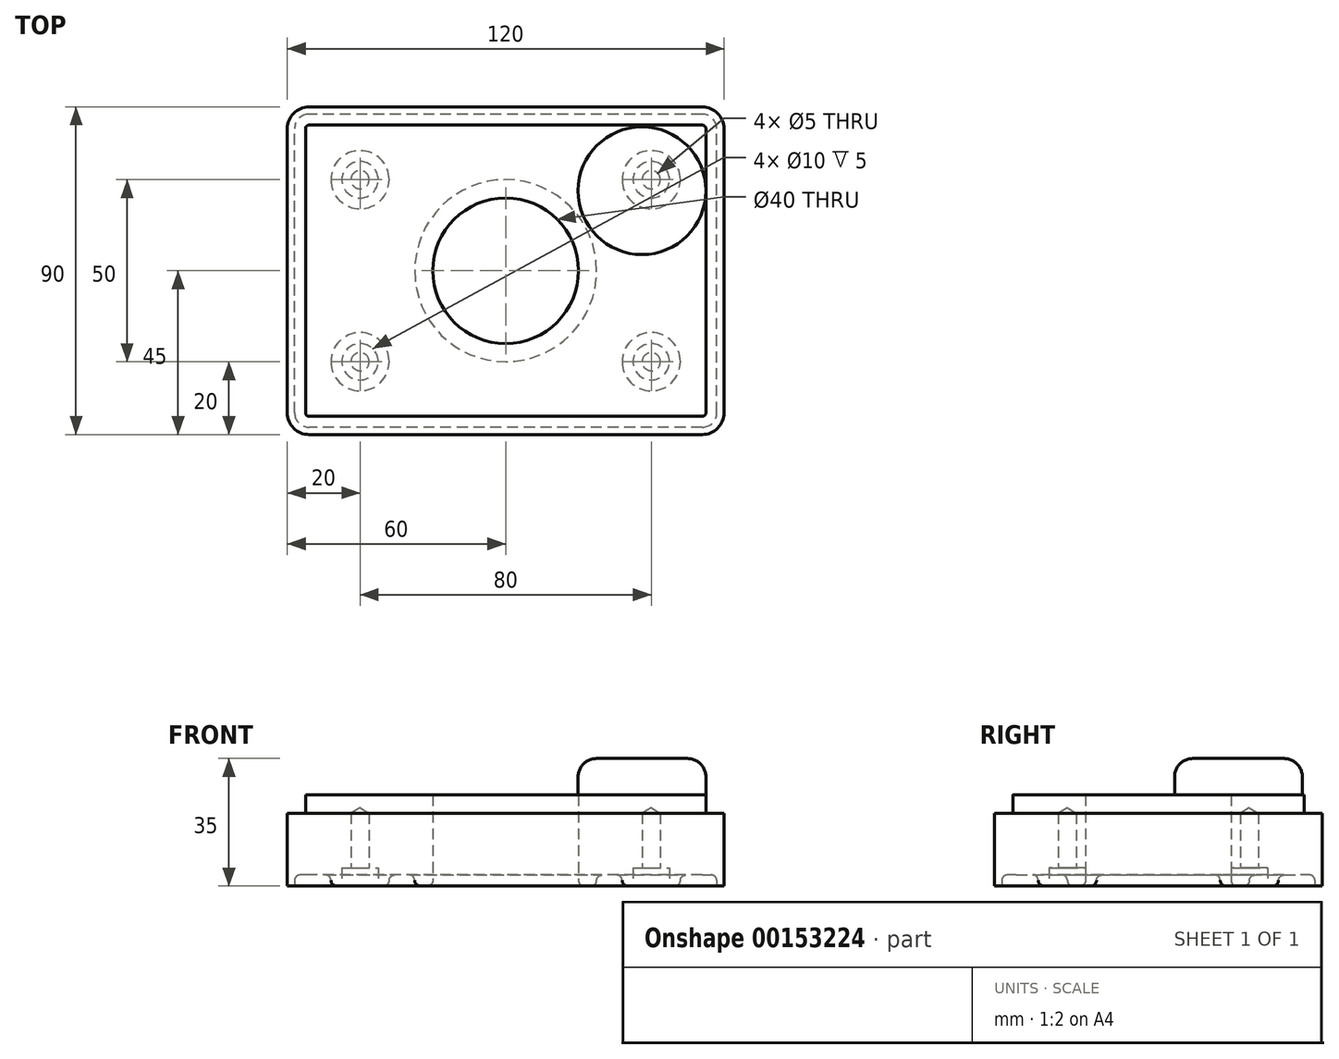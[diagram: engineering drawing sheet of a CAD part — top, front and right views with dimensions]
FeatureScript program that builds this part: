
annotation { "Feature Type Name" : "Feature", "Feature Type Description" : "" }
export const myFeature = defineFeature(function(context is Context, id is Id, definition is map)
    precondition{}
    {
        {
            var Q0;
            Q0=qCreatedBy(makeId("Top.planeOp"),FACE);
            var sketch = newSketch(context, id + "F11", { "sketchPlane" : qUnion([Q0])});
            skLineSegment(sketch, "E0.bottom", {"start": v(54, -45) * mm, "end": v(-54, -45) * mm});
            skLineSegment(sketch, "E0.top", {"start": v(54, 45) * mm, "end": v(-54, 45) * mm});
            skLineSegment(sketch, "E0.left", {"start": v(60, -39) * mm, "end": v(60, 39) * mm});
            skLineSegment(sketch, "E0.right", {"start": v(-60, -39) * mm, "end": v(-60, 39) * mm});
            skPoint(sketch, "E0.middle", {"position": v(0, 0) * mm});
            skCircle(sketch, "E1", {"center": v(0, 0) * mm, "radius": 20 * mm});
            skPoint(sketch, "E2.visualSharp", {"position": v(-60, -45) * mm});
            skArc(sketch, "E2.filletArc", {"start": v(-60, -39) * mm, "mid": v(-58.24, -43.24) * mm, "end": v(-54, -45) * mm});
            skPoint(sketch, "E3.visualSharp", {"position": v(60, -45) * mm});
            skArc(sketch, "E3.filletArc", {"start": v(54, -45) * mm, "mid": v(58.24, -43.24) * mm, "end": v(60, -39) * mm});
            skPoint(sketch, "E4.visualSharp", {"position": v(60, 45) * mm});
            skArc(sketch, "E4.filletArc", {"start": v(60, 39) * mm, "mid": v(58.24, 43.24) * mm, "end": v(54, 45) * mm});
            skPoint(sketch, "E5.visualSharp", {"position": v(-60, 45) * mm});
            skArc(sketch, "E5.filletArc", {"start": v(-54, 45) * mm, "mid": v(-58.24, 43.24) * mm, "end": v(-60, 39) * mm});
            skSolve(sketch);
        }
        {
            var Q0;
            Q0=makeQuery(id+"F11.imprint","IMPRINT",FACE,{"disambiguationData":[TD([[makeQuery(id+"F11.imprint","IMPRINT",EDGE,{"derivedFrom":sQuery(id+"F11.wireOp",EDGE,"E0.bottom")}),-1.0]])]});
            extrude(context, id + "F0", {"entities" : qUnion([Q0]), "depth" : 25 * mm});
        }
        {
            var Q0;
            Q0=makeQuery(id+"F0.opExtrude","CAP_FACE",FACE,{"disambiguationData":[OSD([sQuery(id+"F11.wireOp",EDGE,"E0.bottom"),sQuery(id+"F11.wireOp",EDGE,"E0.top"),sQuery(id+"F11.wireOp",EDGE,"E0.left"),sQuery(id+"F11.wireOp",EDGE,"E0.right"),sQuery(id+"F11.wireOp",EDGE,"E1"),sQuery(id+"F11.wireOp",EDGE,"E2.filletArc"),sQuery(id+"F11.wireOp",EDGE,"E3.filletArc"),sQuery(id+"F11.wireOp",EDGE,"E4.filletArc"),sQuery(id+"F11.wireOp",EDGE,"E5.filletArc")])],"isStart":false});
            var sketch = newSketch(context, id + "F1", { "sketchPlane" : qUnion([Q0])});
            skArc(sketch, "E6.0", {"start": v(54, -40) * mm, "mid": v(54.7, -39.7) * mm, "end": v(55, -39) * mm});
            skLineSegment(sketch, "E6.1", {"start": v(55, -39) * mm, "end": v(55, 39) * mm});
            skLineSegment(sketch, "E6.2", {"start": v(54, -40) * mm, "end": v(-54, -40) * mm});
            skArc(sketch, "E6.3", {"start": v(55, 39) * mm, "mid": v(54.7, 39.7) * mm, "end": v(54, 40) * mm});
            skArc(sketch, "E6.4", {"start": v(-55, -39) * mm, "mid": v(-54.7, -39.7) * mm, "end": v(-54, -40) * mm});
            skLineSegment(sketch, "E6.5", {"start": v(-55, -39) * mm, "end": v(-55, 39) * mm});
            skArc(sketch, "E6.6", {"start": v(-54, 40) * mm, "mid": v(-54.7, 39.7) * mm, "end": v(-55, 39) * mm});
            skLineSegment(sketch, "E6.7", {"start": v(54, 40) * mm, "end": v(-54, 40) * mm});
            skSolve(sketch);
        }
        {
            var Q0;
            Q0=makeQuery(id+"F1.imprint","IMPRINT",FACE,{"disambiguationData":[TD([[makeQuery(id+"F1.imprint","IMPRINT",EDGE,{"derivedFrom":sQuery(id+"F1.wireOp",EDGE,"E6.0")}),-1.0]])]});
            extrude(context, id + "F2", {"entities" : qUnion([Q0]), "operationType" : NewBodyOperationType.REMOVE, "oppositeDirection" : true, "depth" : 5 * mm});
        }
        {
            var Q0;
            Q0=makeQuery(id+"F0.opExtrude","CAP_FACE",FACE,{"disambiguationData":[OSD([sQuery(id+"F11.wireOp",EDGE,"E0.bottom"),sQuery(id+"F11.wireOp",EDGE,"E0.top"),sQuery(id+"F11.wireOp",EDGE,"E0.left"),sQuery(id+"F11.wireOp",EDGE,"E0.right"),sQuery(id+"F11.wireOp",EDGE,"E1"),sQuery(id+"F11.wireOp",EDGE,"E2.filletArc"),sQuery(id+"F11.wireOp",EDGE,"E3.filletArc"),sQuery(id+"F11.wireOp",EDGE,"E4.filletArc"),sQuery(id+"F11.wireOp",EDGE,"E5.filletArc")])],"isStart":true});
            var sketch = newSketch(context, id + "F3", { "sketchPlane" : qUnion([Q0])});
            skPoint(sketch, "E7", {"position": v(40, -25) * mm});
            skPoint(sketch, "E8", {"position": v(-40, -25) * mm});
            skPoint(sketch, "E9", {"position": v(-40, 25) * mm});
            skPoint(sketch, "E10", {"position": v(40, 25) * mm});
            skLineSegment(sketch, "E11", {"start": v(40, -25) * mm, "end": v(40, 0) * mm, "construction": true});
            skLineSegment(sketch, "E12", {"start": v(40, 0) * mm, "end": v(40, 0) * mm});
            skLineSegment(sketch, "E13", {"start": v(40, 25) * mm, "end": v(40, 0) * mm, "construction": true});
            skLineSegment(sketch, "E14", {"start": v(40, 0) * mm, "end": v(0, 0) * mm, "construction": true});
            skLineSegment(sketch, "E15", {"start": v(40, -25) * mm, "end": v(-40, 25) * mm, "construction": true});
            skSolve(sketch);
        }
        {
            var Q0;
            Q0=sQuery(id+"F3.wireOp",VERTEX,"E7");
            var Q1;
            Q1=sQuery(id+"F3.wireOp",VERTEX,"E8");
            var Q2;
            Q2=sQuery(id+"F3.wireOp",VERTEX,"E9");
            var Q3;
            Q3=sQuery(id+"F3.wireOp",VERTEX,"E10");
            var Q4;
            Q4=makeQuery(id+"F0.opExtrude","SWEPT_BODY",BODY,{"disambiguationData":[OSD([sQuery(id+"F11.wireOp",EDGE,"E0.bottom"),sQuery(id+"F11.wireOp",EDGE,"E0.top"),sQuery(id+"F11.wireOp",EDGE,"E0.left"),sQuery(id+"F11.wireOp",EDGE,"E0.right"),sQuery(id+"F11.wireOp",EDGE,"E1"),sQuery(id+"F11.wireOp",EDGE,"E2.filletArc"),sQuery(id+"F11.wireOp",EDGE,"E3.filletArc"),sQuery(id+"F11.wireOp",EDGE,"E4.filletArc"),sQuery(id+"F11.wireOp",EDGE,"E5.filletArc")])]});
            hole(context, id + "F12", {"style" : HoleStyle.C_BORE, "endStyle" : HoleEndStyle.BLIND, "standardTappedOrClearance" : lookupTablePath({ "standard" : "ISO", "size" : "M5", "type" : "Tapped" }), "standardBlindInLast" : lookupTablePath({ "standard" : "ISO", "size" : "M5", "type" : "Tapped" }), "holeDiameter" : 5 * mm, "cBoreDiameter" : 10 * mm, "cBoreDepth" : 5 * mm, "holeDepth" : 20 * mm, "locations" : qUnion([Q0, Q1, Q2, Q3]), "scope" : qUnion([Q4])});
        }
        {
            var Q0;
            Q0=makeQuery(id+"F0.opExtrude","CAP_FACE",FACE,{"disambiguationData":[OSD([sQuery(id+"F11.wireOp",EDGE,"E0.bottom"),sQuery(id+"F11.wireOp",EDGE,"E0.top"),sQuery(id+"F11.wireOp",EDGE,"E0.left"),sQuery(id+"F11.wireOp",EDGE,"E0.right"),sQuery(id+"F11.wireOp",EDGE,"E1"),sQuery(id+"F11.wireOp",EDGE,"E2.filletArc"),sQuery(id+"F11.wireOp",EDGE,"E3.filletArc"),sQuery(id+"F11.wireOp",EDGE,"E4.filletArc"),sQuery(id+"F11.wireOp",EDGE,"E5.filletArc")])],"isStart":true});
            var sketch = newSketch(context, id + "F4", { "sketchPlane" : qUnion([Q0])});
            skCircle(sketch, "E16.0", {"center": v(0, 0) * mm, "radius": 25 * mm});
            skCircle(sketch, "E17.0", {"center": v(-40, 25) * mm, "radius": 8 * mm});
            skCircle(sketch, "E18.0", {"center": v(40, 25) * mm, "radius": 8 * mm});
            skCircle(sketch, "E19.0", {"center": v(40, -25) * mm, "radius": 8 * mm});
            skCircle(sketch, "E20.0", {"center": v(-40, -25) * mm, "radius": 8 * mm});
            skArc(sketch, "E21.0", {"start": v(54, 43) * mm, "mid": v(56.83, 41.83) * mm, "end": v(58, 39) * mm});
            skLineSegment(sketch, "E21.1", {"start": v(58, 39) * mm, "end": v(58, -39) * mm});
            skLineSegment(sketch, "E21.2", {"start": v(54, 43) * mm, "end": v(-54, 43) * mm});
            skArc(sketch, "E21.3", {"start": v(58, -39) * mm, "mid": v(56.83, -41.83) * mm, "end": v(54, -43) * mm});
            skArc(sketch, "E21.4", {"start": v(-58, 39) * mm, "mid": v(-56.83, 41.83) * mm, "end": v(-54, 43) * mm});
            skLineSegment(sketch, "E21.5", {"start": v(-58, 39) * mm, "end": v(-58, -39) * mm});
            skArc(sketch, "E21.6", {"start": v(-54, -43) * mm, "mid": v(-56.83, -41.83) * mm, "end": v(-58, -39) * mm});
            skLineSegment(sketch, "E21.7", {"start": v(54, -43) * mm, "end": v(-54, -43) * mm});
            skSolve(sketch);
        }
        {
            var Q0;
            Q0 = qSketchRegion(id + "F4", true);
            extrude(context, id + "F5", {"entities" : qUnion([Q0]), "operationType" : NewBodyOperationType.REMOVE, "oppositeDirection" : true, "depth" : 3 * mm});
        }
        {
            var Q0;
            Q0=makeQuery(id+"F5.boolean.opBoolean","COPY",FACE,{"derivedFrom":makeQuery(id+"F5.opExtrude","CAP_FACE",FACE,{"disambiguationData":[OSD([sQuery(id+"F4.wireOp",EDGE,"E16.0"),sQuery(id+"F4.wireOp",EDGE,"E17.0"),sQuery(id+"F4.wireOp",EDGE,"E18.0"),sQuery(id+"F4.wireOp",EDGE,"E19.0"),sQuery(id+"F4.wireOp",EDGE,"E20.0"),sQuery(id+"F4.wireOp",EDGE,"E21.0"),sQuery(id+"F4.wireOp",EDGE,"E21.1"),sQuery(id+"F4.wireOp",EDGE,"E21.2"),sQuery(id+"F4.wireOp",EDGE,"E21.3"),sQuery(id+"F4.wireOp",EDGE,"E21.4"),sQuery(id+"F4.wireOp",EDGE,"E21.5"),sQuery(id+"F4.wireOp",EDGE,"E21.6"),sQuery(id+"F4.wireOp",EDGE,"E21.7")])],"isStart":false})});
            var Q1;
            Q1=makeQuery(id+"F5.boolean.opBoolean","COPY",EDGE,{"derivedFrom":makeQuery(id+"F5.opExtrude","CAP_EDGE",EDGE,{"disambiguationData":[OSD([sQuery(id+"F4.wireOp",EDGE,"E16.0")])],"isStart":true})});
            var Q2;
            Q2=makeQuery(id+"F5.boolean.opBoolean","COPY",EDGE,{"derivedFrom":makeQuery(id+"F5.opExtrude","CAP_EDGE",EDGE,{"disambiguationData":[OSD([sQuery(id+"F4.wireOp",EDGE,"E19.0")])],"isStart":true})});
            var Q3;
            Q3=makeQuery(id+"F5.boolean.opBoolean","COPY",EDGE,{"derivedFrom":makeQuery(id+"F5.opExtrude","CAP_EDGE",EDGE,{"disambiguationData":[OSD([sQuery(id+"F4.wireOp",EDGE,"E18.0")])],"isStart":true})});
            var Q4;
            Q4=makeQuery(id+"F5.boolean.opBoolean","COPY",EDGE,{"derivedFrom":makeQuery(id+"F5.opExtrude","CAP_EDGE",EDGE,{"disambiguationData":[OSD([sQuery(id+"F4.wireOp",EDGE,"E17.0")])],"isStart":true})});
            var Q5;
            Q5=makeQuery(id+"F5.boolean.opBoolean","COPY",EDGE,{"derivedFrom":makeQuery(id+"F5.opExtrude","CAP_EDGE",EDGE,{"disambiguationData":[OSD([sQuery(id+"F4.wireOp",EDGE,"E20.0")])],"isStart":true})});
            var Q6;
            Q6=makeQuery(id+"F0.opExtrude","CAP_EDGE",EDGE,{"disambiguationData":[OSD([sQuery(id+"F11.wireOp",EDGE,"E1")])],"isStart":true});
            fillet(context, id + "F6", {"entities" : qUnion([Q0, Q1, Q2, Q3, Q4, Q5, Q6]), "radius" : 1.5 * mm, "tangentPropagation" : true, "allowEdgeOverflow" : false});
        }
        {
            var Q0;
            Q0=makeQuery(id+"F0.opExtrude","CAP_FACE",FACE,{"disambiguationData":[OSD([sQuery(id+"F11.wireOp",EDGE,"E0.bottom"),sQuery(id+"F11.wireOp",EDGE,"E0.top"),sQuery(id+"F11.wireOp",EDGE,"E0.left"),sQuery(id+"F11.wireOp",EDGE,"E0.right"),sQuery(id+"F11.wireOp",EDGE,"E1"),sQuery(id+"F11.wireOp",EDGE,"E2.filletArc"),sQuery(id+"F11.wireOp",EDGE,"E3.filletArc"),sQuery(id+"F11.wireOp",EDGE,"E4.filletArc"),sQuery(id+"F11.wireOp",EDGE,"E5.filletArc")])],"isStart":false});
            var sketch = newSketch(context, id + "F7", { "sketchPlane" : qUnion([Q0])});
            skCircle(sketch, "E22", {"center": v(37.45, 22) * mm, "radius": 17.55 * mm});
            skSolve(sketch);
        }
        {
            var Q0;
            Q0=makeQuery(id+"F7.imprint","IMPRINT",FACE,{"disambiguationData":[TD([[makeQuery(id+"F7.imprint","IMPRINT",EDGE,{"derivedFrom":sQuery(id+"F7.wireOp",EDGE,"E22")}),1.0]])]});
            extrude(context, id + "F13", {"entities" : qUnion([Q0]), "operationType" : NewBodyOperationType.ADD, "depth" : 10 * mm});
        }
        {
            var Q0;
            Q0=makeQuery(id+"F13.opExtrude","CAP_EDGE",EDGE,{"disambiguationData":[OSD([sQuery(id+"F7.wireOp",EDGE,"E22")])],"isStart":false});
            fillet(context, id + "F8", {"entities" : qUnion([Q0]), "radius" : 5 * mm, "tangentPropagation" : true, "allowEdgeOverflow" : false});
        }
        {
            var Q0;
            Q0=makeQuery(id+"F0.opExtrude","CAP_FACE",FACE,{"disambiguationData":[OSD([sQuery(id+"F11.wireOp",EDGE,"E0.bottom"),sQuery(id+"F11.wireOp",EDGE,"E0.top"),sQuery(id+"F11.wireOp",EDGE,"E0.left"),sQuery(id+"F11.wireOp",EDGE,"E0.right"),sQuery(id+"F11.wireOp",EDGE,"E1"),sQuery(id+"F11.wireOp",EDGE,"E2.filletArc"),sQuery(id+"F11.wireOp",EDGE,"E3.filletArc"),sQuery(id+"F11.wireOp",EDGE,"E4.filletArc"),sQuery(id+"F11.wireOp",EDGE,"E5.filletArc")])],"isStart":false});
            var sketch = newSketch(context, id + "F9", { "sketchPlane" : qUnion([Q0])});
            skCircle(sketch, "E23", {"center": v(-35, 0.23) * mm, "radius": 5 * mm});
            skSolve(sketch);
        }
        {
            var Q0;
            Q0 = qSketchRegion(id + "F9", true);
            extrude(context, id + "F14", {"entities" : qUnion([Q0]), "operationType" : NewBodyOperationType.REMOVE, "depth" : 25 * mm});
        }
    });
